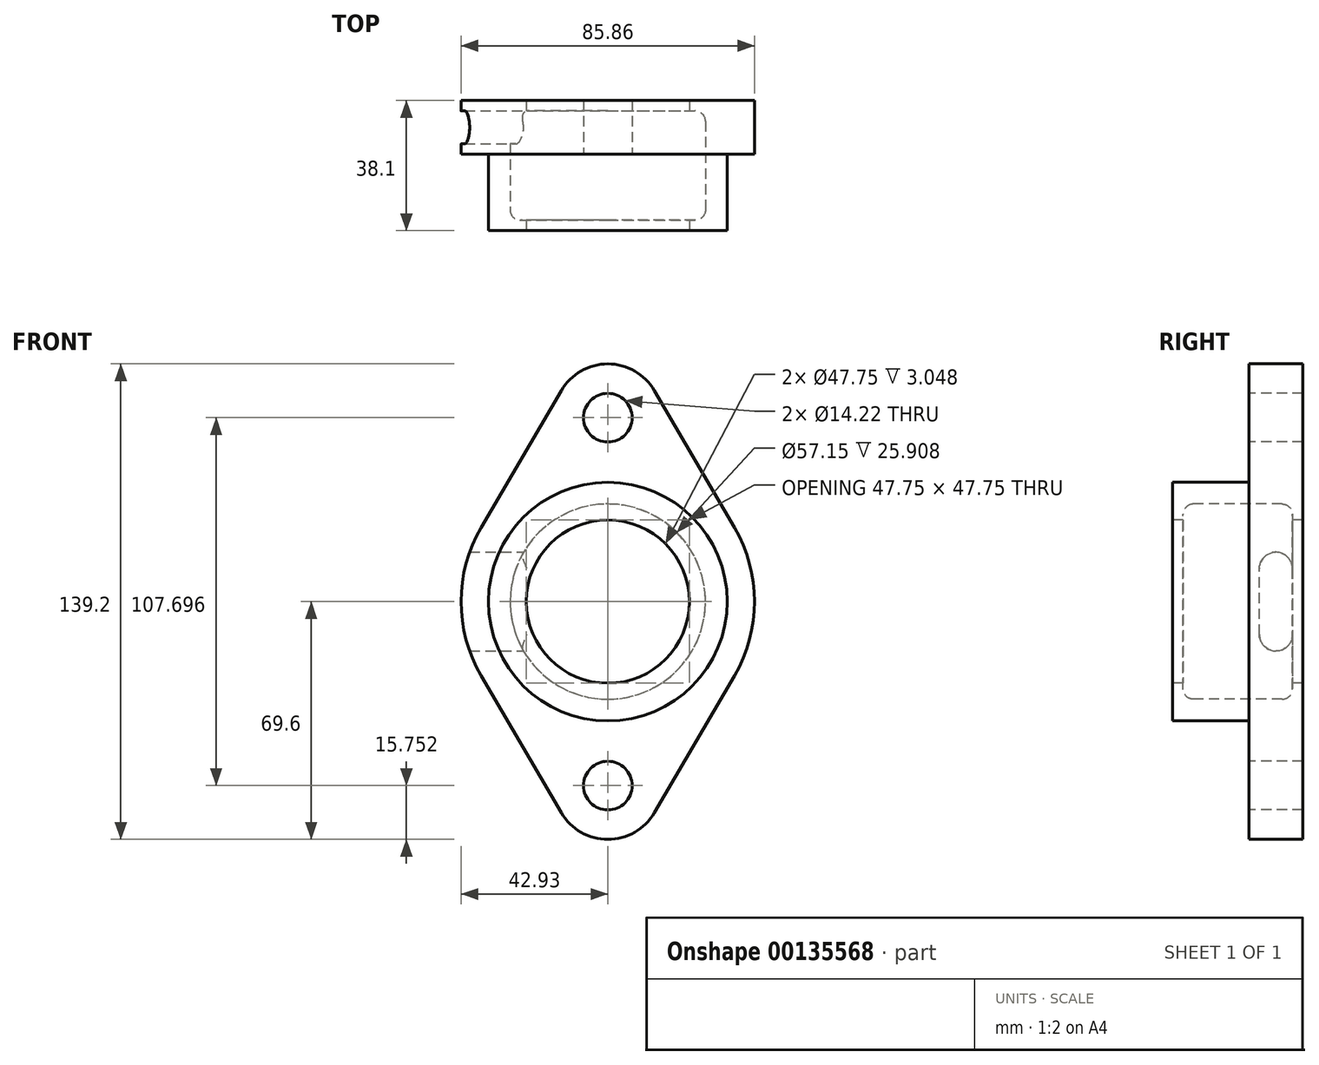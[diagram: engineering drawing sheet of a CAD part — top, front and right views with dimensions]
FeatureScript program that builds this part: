
annotation { "Feature Type Name" : "Feature", "Feature Type Description" : "" }
export const myFeature = defineFeature(function(context is Context, id is Id, definition is map)
    precondition{}
    {
        {
            var Q0;
            Q0=qCreatedBy(makeId("Front.planeOp"),FACE);
            var sketch = newSketch(context, id + "F0", { "sketchPlane" : qUnion([Q0])});
            skArc(sketch, "E0", {"start": v(37.06, -21.67) * mm, "mid": v(42.93, 0) * mm, "end": v(37.06, 21.67) * mm});
            skArc(sketch, "E1", {"start": v(-37.06, 21.67) * mm, "mid": v(-42.93, 0) * mm, "end": v(-37.06, -21.67) * mm});
            skLineSegment(sketch, "E2", {"start": v(-37.06, 21.67) * mm, "end": v(-13.6, 61.8) * mm});
            skLineSegment(sketch, "E3", {"start": v(-37.06, -21.67) * mm, "end": v(-13.6, -61.8) * mm});
            skLineSegment(sketch, "E4", {"start": v(37.06, 21.67) * mm, "end": v(13.6, 61.8) * mm});
            skLineSegment(sketch, "E5", {"start": v(37.06, -21.67) * mm, "end": v(13.6, -61.8) * mm});
            skArc(sketch, "E6", {"start": v(13.6, 61.8) * mm, "mid": v(0, 69.6) * mm, "end": v(-13.6, 61.8) * mm});
            skArc(sketch, "E7", {"start": v(-13.6, -61.8) * mm, "mid": v(0, -69.6) * mm, "end": v(13.6, -61.8) * mm});
            skCircle(sketch, "E8", {"center": v(0, 53.85) * mm, "radius": 7.11 * mm});
            skCircle(sketch, "E9", {"center": v(0, -53.85) * mm, "radius": 7.11 * mm});
            skSolve(sketch);
        }
        {
            var Q0;
            Q0 = qSketchRegion(id + "F0", true);
            extrude(context, id + "F1", {"entities" : qUnion([Q0]), "oppositeDirection" : true, "depth" : 15.75 * mm});
        }
        {
            var Q0;
            Q0=makeQuery(id+"F1.opExtrude","CAP_FACE",FACE,{"disambiguationData":[OSD([sQuery(id+"F0.wireOp",EDGE,"E0"),sQuery(id+"F0.wireOp",EDGE,"E1"),sQuery(id+"F0.wireOp",EDGE,"E2"),sQuery(id+"F0.wireOp",EDGE,"E3"),sQuery(id+"F0.wireOp",EDGE,"E4"),sQuery(id+"F0.wireOp",EDGE,"E5"),sQuery(id+"F0.wireOp",EDGE,"E6"),sQuery(id+"F0.wireOp",EDGE,"E7"),sQuery(id+"F0.wireOp",EDGE,"E8"),sQuery(id+"F0.wireOp",EDGE,"E9")])],"isStart":true});
            var sketch = newSketch(context, id + "F2", { "sketchPlane" : qUnion([Q0])});
            skCircle(sketch, "E10", {"center": v(0, 0) * mm, "radius": 34.93 * mm});
            skSolve(sketch);
        }
        {
            var Q0;
            Q0 = qSketchRegion(id + "F2", true);
            extrude(context, id + "F3", {"entities" : qUnion([Q0]), "operationType" : NewBodyOperationType.ADD, "depth" : 22.35 * mm});
        }
        {
            var Q0;
            Q0=qCreatedBy(makeId("Top.planeOp"),FACE);
            var sketch = newSketch(context, id + "F4", { "sketchPlane" : qUnion([Q0])});
            skLineSegment(sketch, "E11.bottom", {"start": v(-25.53, 12.7) * mm, "end": v(0, 12.7) * mm});
            skLineSegment(sketch, "E11.top", {"start": v(-25.53, -19.3) * mm, "end": v(0, -19.3) * mm});
            skLineSegment(sketch, "E11.left", {"start": v(-28.57, 9.65) * mm, "end": v(-28.57, -16.26) * mm});
            skPoint(sketch, "E12.visualSharp", {"position": v(-28.57, 12.7) * mm});
            skArc(sketch, "E12.filletArc", {"start": v(-25.53, 12.7) * mm, "mid": v(-27.68, 11.8) * mm, "end": v(-28.58, 9.65) * mm});
            skPoint(sketch, "E13.visualSharp", {"position": v(-28.57, -19.3) * mm});
            skArc(sketch, "E13.filletArc", {"start": v(-28.57, -16.26) * mm, "mid": v(-27.68, -18.41) * mm, "end": v(-25.53, -19.3) * mm});
            skLineSegment(sketch, "E14", {"start": v(0, 12.7) * mm, "end": v(0, -19.3) * mm});
            skLineSegment(sketch, "E15", {"start": v(0, 31.56) * mm, "end": v(0, -35.77) * mm, "construction": true});
            skSolve(sketch);
        }
        {
            var Q0;
            Q0=makeQuery(id+"F3.opExtrude","CAP_FACE",FACE,{"disambiguationData":[OSD([sQuery(id+"F2.wireOp",EDGE,"E10")])],"isStart":false});
            var sketch = newSketch(context, id + "F5", { "sketchPlane" : qUnion([Q0])});
            skCircle(sketch, "E16", {"center": v(0, 0) * mm, "radius": 23.88 * mm});
            skSolve(sketch);
        }
        {
            var Q0;
            Q0 = qSketchRegion(id + "F5", true);
            extrude(context, id + "F6", {"entities" : qUnion([Q0]), "operationType" : NewBodyOperationType.REMOVE, "endBound" : BoundingType.THROUGH_ALL, "oppositeDirection" : true, "depth" : 25.4 * mm});
        }
        {
            var Q0;
            Q0 = qSketchRegion(id + "F4", true);
            var Q1;
            Q1=sQuery(id+"F4.wireOp",EDGE,"E15");
            revolve(context, id + "F7", {"operationType" : NewBodyOperationType.REMOVE, "entities" : qUnion([Q0]), "axis" : qUnion([Q1]), "revolveType" : RevolveType.FULL, "oppositeDirection" : true});
        }
        {
            var Q0;
            Q0=qCreatedBy(makeId("Right.planeOp"),FACE);
            var sketch = newSketch(context, id + "F8", { "sketchPlane" : qUnion([Q0])});
            skLineSegment(sketch, "E17", {"start": v(50.09, 0) * mm, "end": v(-60.9, 0) * mm, "construction": true});
            skLineSegment(sketch, "E18", {"start": v(12.7, 9.65) * mm, "end": v(12.7, -9.65) * mm});
            skArc(sketch, "E19", {"start": v(12.7, 9.65) * mm, "mid": v(7.87, 14.48) * mm, "end": v(3.05, 9.65) * mm});
            skArc(sketch, "E20", {"start": v(3.05, -9.65) * mm, "mid": v(7.87, -14.48) * mm, "end": v(12.7, -9.65) * mm});
            skLineSegment(sketch, "E21", {"start": v(3.05, -9.65) * mm, "end": v(3.05, 9.65) * mm});
            skSolve(sketch);
        }
        {
            var Q0;
            Q0 = qSketchRegion(id + "F8", true);
            extrude(context, id + "F9", {"entities" : qUnion([Q0]), "operationType" : NewBodyOperationType.REMOVE, "endBound" : BoundingType.THROUGH_ALL, "oppositeDirection" : true, "depth" : 25.4 * mm});
        }
    });
